# Revit family: Haworth_Riverbend_MeetingBox_EU_PRELIMINARY
name_source: partatom
category: Furniture
units: mm (PartAtom-declared; Revit-internal decimal feet)

## family parameters
Always vertical = Yes
Cut with Voids When Loaded = No
OmniClass Number = 23.40.70.14.64.21
OmniClass Title = Systems Furniture
Room Calculation Point = No
Shared = No
Work Plane-Based = No

## types (6) — shared parameters
Actual Height = 137 cm
Assembly Code = E2020200
Description = Haworth - Riverbend - Meeting Box
Front Finish = Haworth _ Plastic _ Black
Manufacturer = Haworth
Model = SELSBLHX
Revision Number = 1
Size = Verify Final Dim. w/ Haworth
Standard Depths = 261cm
Standard Widths = 144cm, 174cm
TV Mount = Yes
TV Mount Finish = Haworth _ Paint _ Metallic Silver
Trim Finish = Haworth _ Paint _ Plaster
URL = https://www.haworth.com
URL - Product = https://www.haworth.com
Warranty = http://www.haworth.com
With Top = Yes
Without Top = No

## per-type parameters (varying)
| type | Actual Width | Large | Large Top | Medium | Medium Top | Seat Width | Small | Small Top |
| 4 Seater - 52D | 144 cm | No | No | Yes | Yes | 140 cm | No | No |
| 6 Seater - 58D | 174 cm | Yes | Yes | No | No | 170 cm | No | No |
| 4 Seater - 58D | 144 cm | No | No | Yes | Yes | 140 cm | No | No |
| 6 Seater - 52D | 174 cm | Yes | Yes | No | No | 170 cm | No | No |
| 2 Seater - 52D | 74 cm | No | No | No | No | 70 cm | Yes | Yes |
| 2 Seater - 58D | 74 cm | No | No | No | No | 70 cm | Yes | Yes |

## geometry (parser evidence)
native form markers: Sweep x24
no freeform markers — native parametric forms only
